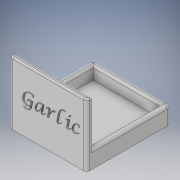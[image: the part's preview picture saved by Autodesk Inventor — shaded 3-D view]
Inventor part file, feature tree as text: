
AUTODESK INVENTOR PART (.ipt)
format: ipt  version: 2019 (Build 230136000, 136)  size: 361,984 bytes
history: native  units: in
note: dims shown in document units (in); Inventor stores cm internally (conversion verified against a paired STEP export)
features: extrude x5, sketch x5, fillet x4
ambient origin geometry x8: Origin, YZ Plane, XZ Plane, XY Plane, X Axis, Y Axis, Z Axis, Center Point
bodies: Solid1 (feature_tree)
feature tree (14):
  extrude  "Extrusion1"  Depth=3.0in
  extrude  "Extrusion2"  TaperAngle=0.0deg  [1 undecoded]
  extrude  "Extrusion3"  Depth=0.1875in
  extrude  "Extrusion6"  Depth=0.1875in
  fillet  "Fillet5"  Radius=2.25in
  fillet  "Fillet7"  [1 undecoded]
  fillet  "Fillet8"  Radius=0.1875in
  extrude  "Extrusion7"  Depth=0.0625in
  fillet  "Fillet9"  [1 undecoded]
  sketch  "Sketch1"  dims[d0=3.0in d1=3.25in]
  sketch  "Sketch2"  dims[d2=0.1875in d3=0.0in]
  sketch  "Sketch3"  dims[d4=0.1875in d5=0.5in]
  sketch  "Sketch6"  dims[d6=0.0in d7=0.1875in d8=2.25in d9=0.0in d17=0.1875in]
  sketch  "Sketch7"  dims[d18=0.1875in d19=0.5in d20=0.0in d22=0.125in d24=0.125in d25=0.125in d26=0.0787in d27=0.0in d28=0.0625in d29=1.35in]
note: 3 required parameter values undecoded (feature->parameter linkage not recoverable at this tier; creation-order binding heuristic only, values carry confidence <= 0.55)
